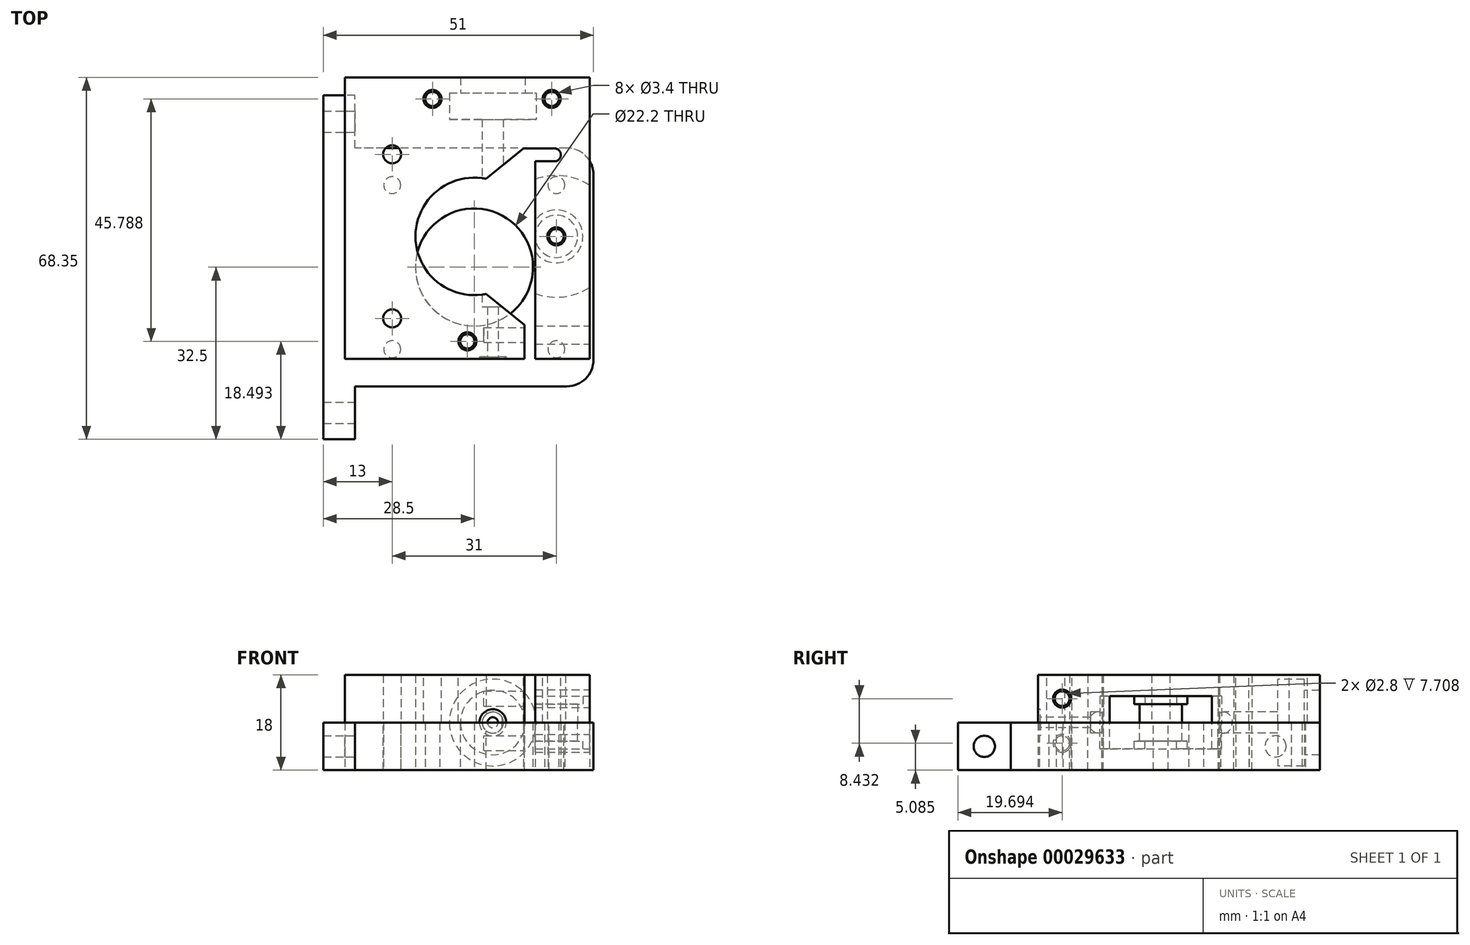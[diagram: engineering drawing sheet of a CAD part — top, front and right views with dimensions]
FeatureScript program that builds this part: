
annotation { "Feature Type Name" : "Feature", "Feature Type Description" : "" }
export const myFeature = defineFeature(function(context is Context, id is Id, definition is map)
    precondition{}
    {
        {
            var Q0;
            Q0=qCreatedBy(makeId("Top.planeOp"),FACE);
            var sketch = newSketch(context, id + "F0", { "sketchPlane" : qUnion([Q0])});
            skLineSegment(sketch, "E0", {"start": v(-24.43, 35.85) * mm, "end": v(-24.43, -17.36) * mm});
            skLineSegment(sketch, "E1", {"start": v(-24.43, -17.36) * mm, "end": v(-24.43, -17.36) * mm});
            skLineSegment(sketch, "E2", {"start": v(-24.43, -17.36) * mm, "end": v(-24.43, -17.35) * mm});
            skLineSegment(sketch, "E3", {"start": v(-24.43, -17.35) * mm, "end": v(9.48, -17.35) * mm});
            skLineSegment(sketch, "E4", {"start": v(9.48, -17.35) * mm, "end": v(9.48, 22.43) * mm});
            skLineSegment(sketch, "E5", {"start": v(9.48, 22.43) * mm, "end": v(15.14, 22.43) * mm});
            skLineSegment(sketch, "E6", {"start": v(15.14, 20) * mm, "end": v(11.48, 20) * mm});
            skLineSegment(sketch, "E7", {"start": v(11.48, 20) * mm, "end": v(11.48, -17.35) * mm});
            skLineSegment(sketch, "E8", {"start": v(11.48, -17.35) * mm, "end": v(21.77, -17.35) * mm});
            skLineSegment(sketch, "E9", {"start": v(21.77, -17.35) * mm, "end": v(21.77, 35.85) * mm});
            skLineSegment(sketch, "E10", {"start": v(21.77, 35.85) * mm, "end": v(-24.43, 35.85) * mm});
            skCircle(sketch, "E11", {"center": v(-7.89, 31.78) * mm, "radius": 1.35 * mm});
            skCircle(sketch, "E12", {"center": v(14.61, 31.78) * mm, "radius": 1.35 * mm});
            skCircle(sketch, "E13", {"center": v(-1.3, -14) * mm, "radius": 1.35 * mm});
            skArc(sketch, "E14", {"start": v(15.14, 20) * mm, "mid": v(16.35, 21.21) * mm, "end": v(15.14, 22.43) * mm});
            skCircle(sketch, "E15", {"center": v(-7.89, 31.78) * mm, "radius": 1.7 * mm});
            skCircle(sketch, "E16", {"center": v(14.61, 31.78) * mm, "radius": 1.7 * mm});
            skCircle(sketch, "E17", {"center": v(-1.3, -14) * mm, "radius": 1.7 * mm});
            skSolve(sketch);
        }
        {
            var Q0;
            Q0=makeQuery(id+"F0.imprint","IMPRINT",FACE,{"disambiguationData":[TD([[makeQuery(id+"F0.imprint","IMPRINT",EDGE,{"derivedFrom":sQuery(id+"F0.wireOp",EDGE,"E0")}),1.0]])]});
            var Q1;
            Q1=makeQuery(id+"F0.imprint","IMPRINT",FACE,{"disambiguationData":[TD([[makeQuery(id+"F0.imprint","IMPRINT",EDGE,{"derivedFrom":sQuery(id+"F0.wireOp",EDGE,"E11")}),-1.0]])]});
            var Q2;
            Q2=makeQuery(id+"F0.imprint","IMPRINT",FACE,{"disambiguationData":[TD([[makeQuery(id+"F0.imprint","IMPRINT",EDGE,{"derivedFrom":sQuery(id+"F0.wireOp",EDGE,"E12")}),-1.0]])]});
            var Q3;
            Q3=makeQuery(id+"F0.imprint","IMPRINT",FACE,{"disambiguationData":[TD([[makeQuery(id+"F0.imprint","IMPRINT",EDGE,{"derivedFrom":sQuery(id+"F0.wireOp",EDGE,"E13")}),-1.0]])]});
            extrude(context, id + "F1", {"entities" : qUnion([Q0, Q1, Q2, Q3]), "depth" : 9 * mm});
        }
        {
            var Q0;
            Q0=makeQuery(id+"F1.opExtrude","CAP_FACE",FACE,{"disambiguationData":[OSD([sQuery(id+"F0.wireOp",EDGE,"E0"),sQuery(id+"F0.wireOp",EDGE,"E1"),sQuery(id+"F0.wireOp",EDGE,"E2"),sQuery(id+"F0.wireOp",EDGE,"E3"),sQuery(id+"F0.wireOp",EDGE,"E4"),sQuery(id+"F0.wireOp",EDGE,"E5"),sQuery(id+"F0.wireOp",EDGE,"E6"),sQuery(id+"F0.wireOp",EDGE,"E7"),sQuery(id+"F0.wireOp",EDGE,"E8"),sQuery(id+"F0.wireOp",EDGE,"E9"),sQuery(id+"F0.wireOp",EDGE,"E10"),sQuery(id+"F0.wireOp",EDGE,"604cad85-587a-4b7d-8070-06f4cba85480"),sQuery(id+"F0.wireOp",EDGE,"6e5e38c1-5bff-4efe-a8c5-b84022f0a049"),sQuery(id+"F0.wireOp",EDGE,"b8144507-9dd7-4af4-87a3-7b649dd00ae6"),sQuery(id+"F0.wireOp",EDGE,"b9c2cb7c-5e58-4995-888e-a78f0403fbb5"),sQuery(id+"F0.wireOp",EDGE,"885990ab-7576-4c23-8475-595d2769e284"),sQuery(id+"F0.wireOp",EDGE,"E11"),sQuery(id+"F0.wireOp",EDGE,"E12"),sQuery(id+"F0.wireOp",EDGE,"E13"),sQuery(id+"F0.wireOp",EDGE,"E14")])],"isStart":false});
            var sketch = newSketch(context, id + "F2", { "sketchPlane" : qUnion([Q0])});
            skCircle(sketch, "E18", {"center": v(0, 5.82) * mm, "radius": 11.1 * mm});
            skCircle(sketch, "E19", {"center": v(-15.5, 21.32) * mm, "radius": 1.7 * mm});
            skCircle(sketch, "E20", {"center": v(-15.5, -9.68) * mm, "radius": 1.7 * mm});
            skSolve(sketch);
        }
        {
            var Q0;
            Q0=qSketchRegion(id+"F2",true);
            extrude(context, id + "F3", {"entities" : qUnion([Q0]), "operationType" : NewBodyOperationType.REMOVE, "endBound" : BoundingType.THROUGH_ALL, "oppositeDirection" : true, "depth" : 25 * mm});
        }
        {
            var Q0;
            Q0=makeQuery(id+"F1.opExtrude","CAP_FACE",FACE,{"disambiguationData":[OSD([sQuery(id+"F0.wireOp",EDGE,"E0"),sQuery(id+"F0.wireOp",EDGE,"E1"),sQuery(id+"F0.wireOp",EDGE,"E2"),sQuery(id+"F0.wireOp",EDGE,"E3"),sQuery(id+"F0.wireOp",EDGE,"E4"),sQuery(id+"F0.wireOp",EDGE,"E5"),sQuery(id+"F0.wireOp",EDGE,"E6"),sQuery(id+"F0.wireOp",EDGE,"E7"),sQuery(id+"F0.wireOp",EDGE,"E8"),sQuery(id+"F0.wireOp",EDGE,"E9"),sQuery(id+"F0.wireOp",EDGE,"E10"),sQuery(id+"F0.wireOp",EDGE,"604cad85-587a-4b7d-8070-06f4cba85480"),sQuery(id+"F0.wireOp",EDGE,"6e5e38c1-5bff-4efe-a8c5-b84022f0a049"),sQuery(id+"F0.wireOp",EDGE,"E11"),sQuery(id+"F0.wireOp",EDGE,"E12"),sQuery(id+"F0.wireOp",EDGE,"E13"),sQuery(id+"F0.wireOp",EDGE,"E14")])],"isStart":false});
            var sketch = newSketch(context, id + "F4", { "sketchPlane" : qUnion([Q0])});
            skCircle(sketch, "E21", {"center": v(15.5, 5.82) * mm, "radius": 11.5 * mm});
            skCircle(sketch, "E22", {"center": v(15.5, 5.82) * mm, "radius": 5 * mm});
            skCircle(sketch, "E23", {"center": v(15.5, 5.82) * mm, "radius": 4 * mm});
            skLineSegment(sketch, "E24", {"start": v(0, 5.82) * mm, "end": v(31, 5.82) * mm, "construction": true});
            skCircle(sketch, "E25", {"center": v(15.5, 5.82) * mm, "radius": 1.4 * mm});
            skCircle(sketch, "E26", {"center": v(15.5, 5.82) * mm, "radius": 1.7 * mm});
            skSolve(sketch);
        }
        {
            var Q0;
            Q0=makeQuery(id+"F4.imprint","IMPRINT",FACE,{"disambiguationData":[TD([[makeQuery(id+"F4.imprint","IMPRINT",EDGE,{"derivedFrom":sQuery(id+"F4.wireOp",EDGE,"E22")}),-1.0]])]});
            extrude(context, id + "F5", {"entities" : qUnion([Q0]), "operationType" : NewBodyOperationType.REMOVE, "oppositeDirection" : true, "depth" : 5 * mm});
        }
        {
            var Q0;
            Q0=makeQuery(id+"F4.imprint","IMPRINT",FACE,{"disambiguationData":[TD([[makeQuery(id+"F4.imprint","IMPRINT",EDGE,{"derivedFrom":sQuery(id+"F4.wireOp",EDGE,"E22")}),1.0]])]});
            var Q1;
            Q1=makeQuery(id+"F4.imprint","IMPRINT",FACE,{"disambiguationData":[TD([[makeQuery(id+"F4.imprint","IMPRINT",EDGE,{"derivedFrom":sQuery(id+"F4.wireOp",EDGE,"E23")}),-1.0]])]});
            extrude(context, id + "F6", {"entities" : qUnion([Q0, Q1]), "operationType" : NewBodyOperationType.REMOVE, "oppositeDirection" : true, "depth" : 3.5 * mm});
        }
        {
            var Q0;
            {var subQ0=sQuery(id+"F0.wireOp",EDGE,"E0");var subQ1=sQuery(id+"F0.wireOp",EDGE,"E1");var subQ2=sQuery(id+"F0.wireOp",EDGE,"E2");var subQ3=sQuery(id+"F0.wireOp",EDGE,"E3");var subQ4=sQuery(id+"F0.wireOp",EDGE,"E4");var subQ5=sQuery(id+"F0.wireOp",EDGE,"E5");var subQ6=sQuery(id+"F0.wireOp",EDGE,"E6");var subQ7=sQuery(id+"F0.wireOp",EDGE,"E7");var subQ8=sQuery(id+"F0.wireOp",EDGE,"E9");var subQ9=sQuery(id+"F0.wireOp",EDGE,"E10");var subQ10=sQuery(id+"F0.wireOp",EDGE,"604cad85-587a-4b7d-8070-06f4cba85480");var subQ11=sQuery(id+"F0.wireOp",EDGE,"6e5e38c1-5bff-4efe-a8c5-b84022f0a049");var subQ12=sQuery(id+"F0.wireOp",EDGE,"E11");var subQ13=sQuery(id+"F0.wireOp",EDGE,"E12");var subQ14=sQuery(id+"F0.wireOp",EDGE,"E13");var subQ15=sQuery(id+"F0.wireOp",EDGE,"E14");Q0=makeQuery(id+"F5.boolean.opBoolean","SPLIT",FACE,{"disambiguationData":[TD([makeQuery(id+"F1.opExtrude","SWEPT_FACE",FACE,{"disambiguationData":[OSD([subQ0])]})])],"derivedFrom":makeQuery(id+"F1.opExtrude","CAP_FACE",FACE,{"disambiguationData":[OSD([subQ0,subQ1,subQ2,subQ3,subQ4,subQ5,subQ6,subQ7,sQuery(id+"F0.wireOp",EDGE,"E8"),subQ8,subQ9,subQ10,subQ11,subQ12,subQ13,subQ14,subQ15])],"isStart":false})});}
            var sketch = newSketch(context, id + "F7", { "sketchPlane" : qUnion([Q0])});
            skLineSegment(sketch, "E27", {"start": v(3.5, 15.43) * mm, "end": v(3.5, 37.1) * mm});
            skLineSegment(sketch, "E28", {"start": v(0, 5.82) * mm, "end": v(31.4, 5.82) * mm, "construction": true});
            skLineSegment(sketch, "E29.0.MirrorCS", {"start": v(0.98, -16.94) * mm, "end": v(2.5, -16.94) * mm});
            skLineSegment(sketch, "E29.1.MirrorCS", {"start": v(3.5, -3.78) * mm, "end": v(3.5, -25.46) * mm});
            skLineSegment(sketch, "E29.2.MirrorCS", {"start": v(0.98, -25.46) * mm, "end": v(0.98, -16.94) * mm});
            skLineSegment(sketch, "E29.3.MirrorCS", {"start": v(1.5, -3.78) * mm, "end": v(3.5, -3.78) * mm});
            skLineSegment(sketch, "E29.4.MirrorCS", {"start": v(2.5, -7.47) * mm, "end": v(1.5, -7.47) * mm});
            skLineSegment(sketch, "E29.5.MirrorCS", {"start": v(2.5, -16.94) * mm, "end": v(2.5, -7.47) * mm});
            skLineSegment(sketch, "E29.6.MirrorCS", {"start": v(3.5, -25.46) * mm, "end": v(0.98, -25.46) * mm});
            skLineSegment(sketch, "E30", {"start": v(-2.6, 37.1) * mm, "end": v(-2.6, 32.9) * mm});
            skLineSegment(sketch, "E31", {"start": v(-2.6, 32.9) * mm, "end": v(-4.7, 32.9) * mm});
            skLineSegment(sketch, "E32", {"start": v(-4.7, 32.9) * mm, "end": v(-4.7, 27.9) * mm});
            skLineSegment(sketch, "E33", {"start": v(-4.7, 27.9) * mm, "end": v(1.5, 27.9) * mm});
            skLineSegment(sketch, "E34", {"start": v(-2.6, 37.1) * mm, "end": v(3.5, 37.1) * mm});
            skLineSegment(sketch, "E35", {"start": v(1.5, 27.9) * mm, "end": v(1.5, 15.43) * mm});
            skLineSegment(sketch, "E36", {"start": v(1.5, 15.43) * mm, "end": v(3.5, 15.43) * mm});
            skLineSegment(sketch, "E37", {"start": v(1.5, -7.47) * mm, "end": v(1.5, -3.78) * mm});
            skSolve(sketch);
        }
        {
            var Q0;
            Q0=qSketchRegion(id+"F7",true);
            var Q1;
            Q1=sQuery(id+"F7.wireOp",EDGE,"E27");
            revolve(context, id + "F8", {"entities" : qUnion([Q0]), "axis" : qUnion([Q1]), "revolveType" : RevolveType.FULL});
        }
        {
            var Q0;
            Q0=makeQuery(id+"F8.opRevolve","SWEPT_BODY",BODY,{"disambiguationData":[OSD([sQuery(id+"F7.wireOp",EDGE,"0e4a01cc-4869-4b9d-8ca2-1c94110d196d"),sQuery(id+"F7.wireOp",EDGE,"4d913e13-2244-4a79-84d2-82f6c5de00b3"),sQuery(id+"F7.wireOp",EDGE,"1203443b-fa58-4cec-9fe4-144960d3b7c2"),sQuery(id+"F7.wireOp",EDGE,"f73e5a92-9274-40af-91db-ab5fa52ec61f"),sQuery(id+"F7.wireOp",EDGE,"4cc6588a-36a6-4115-9f4e-735cf5f17870"),sQuery(id+"F7.wireOp",EDGE,"E27"),sQuery(id+"F7.wireOp",EDGE,"0bbee7b9-97e0-41c3-ac0e-625151f8027d")])]});
            var Q1;
            Q1=makeQuery(id+"F1.opExtrude","SWEPT_BODY",BODY,{"disambiguationData":[OSD([sQuery(id+"F0.wireOp",EDGE,"E0"),sQuery(id+"F0.wireOp",EDGE,"E1"),sQuery(id+"F0.wireOp",EDGE,"E2"),sQuery(id+"F0.wireOp",EDGE,"E3"),sQuery(id+"F0.wireOp",EDGE,"E4"),sQuery(id+"F0.wireOp",EDGE,"E5"),sQuery(id+"F0.wireOp",EDGE,"E6"),sQuery(id+"F0.wireOp",EDGE,"E7"),sQuery(id+"F0.wireOp",EDGE,"E8"),sQuery(id+"F0.wireOp",EDGE,"E9"),sQuery(id+"F0.wireOp",EDGE,"E10"),sQuery(id+"F0.wireOp",EDGE,"604cad85-587a-4b7d-8070-06f4cba85480"),sQuery(id+"F0.wireOp",EDGE,"6e5e38c1-5bff-4efe-a8c5-b84022f0a049"),sQuery(id+"F0.wireOp",EDGE,"E11"),sQuery(id+"F0.wireOp",EDGE,"E12"),sQuery(id+"F0.wireOp",EDGE,"E13"),sQuery(id+"F0.wireOp",EDGE,"E14")])]});
            booleanBodies(context, id + "F9", {"operationType" : BooleanOperationType.SUBTRACTION, "tools" : qUnion([Q0]), "targets" : qUnion([Q1]), "keepTools" : true});
        }
        {
            var Q0;
            Q0=makeQuery(id+"F8.opRevolve","SWEPT_BODY",BODY,{"disambiguationData":[OSD([sQuery(id+"F7.wireOp",EDGE,"E29.0.MirrorCS"),sQuery(id+"F7.wireOp",EDGE,"E29.1.MirrorCS"),sQuery(id+"F7.wireOp",EDGE,"E29.2.MirrorCS"),sQuery(id+"F7.wireOp",EDGE,"E29.3.MirrorCS"),sQuery(id+"F7.wireOp",EDGE,"E29.4.MirrorCS"),sQuery(id+"F7.wireOp",EDGE,"E29.5.MirrorCS"),sQuery(id+"F7.wireOp",EDGE,"E29.6.MirrorCS")])]});
            var Q1;
            Q1=makeQuery(id+"F1.opExtrude","SWEPT_BODY",BODY,{"disambiguationData":[OSD([sQuery(id+"F0.wireOp",EDGE,"E0"),sQuery(id+"F0.wireOp",EDGE,"E1"),sQuery(id+"F0.wireOp",EDGE,"E2"),sQuery(id+"F0.wireOp",EDGE,"E3"),sQuery(id+"F0.wireOp",EDGE,"E4"),sQuery(id+"F0.wireOp",EDGE,"E5"),sQuery(id+"F0.wireOp",EDGE,"E6"),sQuery(id+"F0.wireOp",EDGE,"E7"),sQuery(id+"F0.wireOp",EDGE,"E8"),sQuery(id+"F0.wireOp",EDGE,"E9"),sQuery(id+"F0.wireOp",EDGE,"E10"),sQuery(id+"F0.wireOp",EDGE,"604cad85-587a-4b7d-8070-06f4cba85480"),sQuery(id+"F0.wireOp",EDGE,"6e5e38c1-5bff-4efe-a8c5-b84022f0a049"),sQuery(id+"F0.wireOp",EDGE,"E11"),sQuery(id+"F0.wireOp",EDGE,"E12"),sQuery(id+"F0.wireOp",EDGE,"E13"),sQuery(id+"F0.wireOp",EDGE,"E14")])]});
            booleanBodies(context, id + "F10", {"operationType" : BooleanOperationType.SUBTRACTION, "tools" : qUnion([Q0]), "targets" : qUnion([Q1]), "keepTools" : true});
        }
        {
            var Q0;
            Q0=qSketchRegion(id+"F0",true);
            extrude(context, id + "F11", {"entities" : qUnion([Q0]), "oppositeDirection" : true, "depth" : 9 * mm});
        }
        {
            var Q0;
            Q0=makeQuery(id+"F11.opExtrude","SWEPT_BODY",BODY,{"disambiguationData":[OSD([sQuery(id+"F0.wireOp",EDGE,"E0"),sQuery(id+"F0.wireOp",EDGE,"E3"),sQuery(id+"F0.wireOp",EDGE,"E4"),sQuery(id+"F0.wireOp",EDGE,"E5"),sQuery(id+"F0.wireOp",EDGE,"E6"),sQuery(id+"F0.wireOp",EDGE,"E7"),sQuery(id+"F0.wireOp",EDGE,"E8"),sQuery(id+"F0.wireOp",EDGE,"E9"),sQuery(id+"F0.wireOp",EDGE,"E10"),sQuery(id+"F0.wireOp",EDGE,"E11"),sQuery(id+"F0.wireOp",EDGE,"E12"),sQuery(id+"F0.wireOp",EDGE,"E13"),sQuery(id+"F0.wireOp",EDGE,"E14")])]});
            transform(context, id + "F12", {"entities" : qUnion([Q0]), "transformType" : TransformType.TRANSLATION_3D, "dx" : 0 * mm, "dy" : 0 * mm, "dz" : 18 * mm, "makeCopy" : false});
        }
        {
            var Q0;
            Q0=qSketchRegion(id+"F2",true);
            extrude(context, id + "F13", {"entities" : qUnion([Q0]), "operationType" : NewBodyOperationType.REMOVE, "endBound" : BoundingType.THROUGH_ALL, "depth" : 25 * mm});
        }
        {
            var Q0;
            {var subQ3=sQuery(id+"F4.wireOp",EDGE,"E21");var subQ7=makeQuery(id+"F1.opExtrude","CAP_EDGE",EDGE,{"disambiguationData":[OSD([sQuery(id+"F0.wireOp",EDGE,"E9")])],"isStart":false});var subQ9=makeQuery(id+"F4.imprint","INTERSECT",VERTEX,{"disambiguationData":[OD(0.0)],"derivedFrom":[subQ7,subQ3]});Q0=makeQuery(id+"F4.imprint","IMPRINT",FACE,{"disambiguationData":[TD([[makeQuery(id+"F4.imprint","IMPRINT",EDGE,{"disambiguationData":[TD([[subQ9,-1.0]])],"derivedFrom":subQ3}),1.0]])]});}
            extrude(context, id + "F14", {"entities" : qUnion([Q0]), "operationType" : NewBodyOperationType.REMOVE, "depth" : 5 * mm});
        }
        {
            var Q0;
            Q0=makeQuery(id+"F4.imprint","IMPRINT",FACE,{"disambiguationData":[TD([[makeQuery(id+"F4.imprint","IMPRINT",EDGE,{"derivedFrom":sQuery(id+"F4.wireOp",EDGE,"E23")}),-1.0]])]});
            extrude(context, id + "F15", {"entities" : qUnion([Q0]), "operationType" : NewBodyOperationType.REMOVE, "depth" : 3.5 * mm});
        }
        {
            var Q0;
            Q0=makeQuery(id+"F8.opRevolve","SWEPT_BODY",BODY,{"disambiguationData":[OSD([sQuery(id+"F7.wireOp",EDGE,"0e4a01cc-4869-4b9d-8ca2-1c94110d196d"),sQuery(id+"F7.wireOp",EDGE,"4d913e13-2244-4a79-84d2-82f6c5de00b3"),sQuery(id+"F7.wireOp",EDGE,"1203443b-fa58-4cec-9fe4-144960d3b7c2"),sQuery(id+"F7.wireOp",EDGE,"f73e5a92-9274-40af-91db-ab5fa52ec61f"),sQuery(id+"F7.wireOp",EDGE,"4cc6588a-36a6-4115-9f4e-735cf5f17870"),sQuery(id+"F7.wireOp",EDGE,"E27"),sQuery(id+"F7.wireOp",EDGE,"0bbee7b9-97e0-41c3-ac0e-625151f8027d")])]});
            var Q1;
            Q1=makeQuery(id+"F11.opExtrude","SWEPT_BODY",BODY,{"disambiguationData":[OSD([sQuery(id+"F0.wireOp",EDGE,"E0"),sQuery(id+"F0.wireOp",EDGE,"E3"),sQuery(id+"F0.wireOp",EDGE,"E4"),sQuery(id+"F0.wireOp",EDGE,"E5"),sQuery(id+"F0.wireOp",EDGE,"E6"),sQuery(id+"F0.wireOp",EDGE,"E7"),sQuery(id+"F0.wireOp",EDGE,"E8"),sQuery(id+"F0.wireOp",EDGE,"E9"),sQuery(id+"F0.wireOp",EDGE,"E10"),sQuery(id+"F0.wireOp",EDGE,"E11"),sQuery(id+"F0.wireOp",EDGE,"E12"),sQuery(id+"F0.wireOp",EDGE,"E13"),sQuery(id+"F0.wireOp",EDGE,"E14")])]});
            booleanBodies(context, id + "F16", {"operationType" : BooleanOperationType.SUBTRACTION, "tools" : qUnion([Q0]), "targets" : qUnion([Q1])});
        }
        {
            var Q0;
            Q0=makeQuery(id+"F8.opRevolve","SWEPT_BODY",BODY,{"disambiguationData":[OSD([sQuery(id+"F7.wireOp",EDGE,"E29.0.MirrorCS"),sQuery(id+"F7.wireOp",EDGE,"E29.1.MirrorCS"),sQuery(id+"F7.wireOp",EDGE,"E29.2.MirrorCS"),sQuery(id+"F7.wireOp",EDGE,"E29.3.MirrorCS"),sQuery(id+"F7.wireOp",EDGE,"E29.4.MirrorCS"),sQuery(id+"F7.wireOp",EDGE,"E29.5.MirrorCS"),sQuery(id+"F7.wireOp",EDGE,"E29.6.MirrorCS")])]});
            var Q1;
            Q1=makeQuery(id+"F11.opExtrude","SWEPT_BODY",BODY,{"disambiguationData":[OSD([sQuery(id+"F0.wireOp",EDGE,"E0"),sQuery(id+"F0.wireOp",EDGE,"E3"),sQuery(id+"F0.wireOp",EDGE,"E4"),sQuery(id+"F0.wireOp",EDGE,"E5"),sQuery(id+"F0.wireOp",EDGE,"E6"),sQuery(id+"F0.wireOp",EDGE,"E7"),sQuery(id+"F0.wireOp",EDGE,"E8"),sQuery(id+"F0.wireOp",EDGE,"E9"),sQuery(id+"F0.wireOp",EDGE,"E10"),sQuery(id+"F0.wireOp",EDGE,"E11"),sQuery(id+"F0.wireOp",EDGE,"E12"),sQuery(id+"F0.wireOp",EDGE,"E13"),sQuery(id+"F0.wireOp",EDGE,"E14")])]});
            booleanBodies(context, id + "F17", {"operationType" : BooleanOperationType.SUBTRACTION, "tools" : qUnion([Q0]), "targets" : qUnion([Q1])});
        }
        {
            var Q0;
            Q0=makeQuery(id+"F11.opExtrude","SWEPT_FACE",FACE,{"disambiguationData":[OSD([sQuery(id+"F0.wireOp",EDGE,"E9")])]});
            var sketch = newSketch(context, id + "F18", { "sketchPlane" : qUnion([Q0])});
            skCircle(sketch, "E38", {"center": v(-12.8, 13.52) * mm, "radius": 1.7 * mm});
            skCircle(sketch, "E39", {"center": v(-12.8, 13.52) * mm, "radius": 1.4 * mm});
            skCircle(sketch, "E40", {"center": v(-12.8, 5.09) * mm, "radius": 1.7 * mm});
            skCircle(sketch, "E41", {"center": v(-12.8, 5.09) * mm, "radius": 1.4 * mm});
            skSolve(sketch);
        }
        {
            var Q0;
            Q0=makeQuery(id+"F18.imprint","IMPRINT",FACE,{"disambiguationData":[TD([[makeQuery(id+"F18.imprint","IMPRINT",EDGE,{"derivedFrom":sQuery(id+"F18.wireOp",EDGE,"E39")}),1.0]])]});
            extrude(context, id + "F19", {"entities" : qUnion([Q0]), "operationType" : NewBodyOperationType.REMOVE, "oppositeDirection" : true, "depth" : 20 * mm});
        }
        {
            var Q0;
            Q0=makeQuery(id+"F18.imprint","IMPRINT",FACE,{"disambiguationData":[TD([[makeQuery(id+"F18.imprint","IMPRINT",EDGE,{"derivedFrom":sQuery(id+"F18.wireOp",EDGE,"E38")}),1.0]])]});
            extrude(context, id + "F20", {"entities" : qUnion([Q0]), "operationType" : NewBodyOperationType.REMOVE, "oppositeDirection" : true, "depth" : 11 * mm});
        }
        {
            var Q0;
            Q0=makeQuery(id+"F18.imprint","IMPRINT",FACE,{"disambiguationData":[TD([[makeQuery(id+"F18.imprint","IMPRINT",EDGE,{"derivedFrom":sQuery(id+"F18.wireOp",EDGE,"E41")}),1.0]])]});
            extrude(context, id + "F21", {"entities" : qUnion([Q0]), "operationType" : NewBodyOperationType.REMOVE, "oppositeDirection" : true, "depth" : 20 * mm});
        }
        {
            var Q0;
            Q0=makeQuery(id+"F18.imprint","IMPRINT",FACE,{"disambiguationData":[TD([[makeQuery(id+"F18.imprint","IMPRINT",EDGE,{"derivedFrom":sQuery(id+"F18.wireOp",EDGE,"E40")}),1.0]])]});
            extrude(context, id + "F22", {"entities" : qUnion([Q0]), "operationType" : NewBodyOperationType.REMOVE, "oppositeDirection" : true, "depth" : 11 * mm});
        }
        {
            var Q0;
            Q0=makeQuery(id+"F4.imprint","IMPRINT",FACE,{"disambiguationData":[TD([[makeQuery(id+"F4.imprint","IMPRINT",EDGE,{"derivedFrom":sQuery(id+"F4.wireOp",EDGE,"E25")}),1.0]])]});
            extrude(context, id + "F23", {"entities" : qUnion([Q0]), "operationType" : NewBodyOperationType.REMOVE, "endBound" : BoundingType.THROUGH_ALL, "oppositeDirection" : true, "depth" : 25 * mm});
        }
        {
            var Q0;
            Q0=makeQuery(id+"F4.imprint","IMPRINT",FACE,{"disambiguationData":[TD([[makeQuery(id+"F4.imprint","IMPRINT",EDGE,{"derivedFrom":sQuery(id+"F4.wireOp",EDGE,"E25")}),1.0]])]});
            var Q1;
            Q1=makeQuery(id+"F4.imprint","IMPRINT",FACE,{"disambiguationData":[TD([[makeQuery(id+"F4.imprint","IMPRINT",EDGE,{"derivedFrom":sQuery(id+"F4.wireOp",EDGE,"E25")}),-1.0]])]});
            extrude(context, id + "F24", {"entities" : qUnion([Q0, Q1]), "operationType" : NewBodyOperationType.REMOVE, "endBound" : BoundingType.THROUGH_ALL, "depth" : 25 * mm});
        }
        {
            var Q0;
            Q0=makeQuery(id+"F3.boolean.opBoolean","INTERSECT",EDGE,{"disambiguationData":[OD(0.0)],"derivedFrom":[makeQuery(id+"F1.opExtrude","SWEPT_FACE",FACE,{"disambiguationData":[OSD([sQuery(id+"F0.wireOp",EDGE,"E4")])]}),makeQuery(id+"F3.opExtrude","SWEPT_FACE",FACE,{"disambiguationData":[OSD([sQuery(id+"F2.wireOp",EDGE,"E18")])]})]});
            var Q1;
            Q1=makeQuery(id+"F3.boolean.opBoolean","INTERSECT",EDGE,{"disambiguationData":[OD(1.0)],"derivedFrom":[makeQuery(id+"F1.opExtrude","SWEPT_FACE",FACE,{"disambiguationData":[OSD([sQuery(id+"F0.wireOp",EDGE,"E4")])]}),makeQuery(id+"F3.opExtrude","SWEPT_FACE",FACE,{"disambiguationData":[OSD([sQuery(id+"F2.wireOp",EDGE,"E18")])]})]});
            var Q2;
            Q2=makeQuery(id+"F13.boolean.opBoolean","INTERSECT",EDGE,{"disambiguationData":[OD(1.0)],"derivedFrom":[makeQuery(id+"F11.opExtrude","SWEPT_FACE",FACE,{"disambiguationData":[OSD([sQuery(id+"F0.wireOp",EDGE,"E4")])]}),makeQuery(id+"F13.opExtrude","SWEPT_FACE",FACE,{"disambiguationData":[OSD([sQuery(id+"F2.wireOp",EDGE,"E18")])]})]});
            var Q3;
            Q3=makeQuery(id+"F13.boolean.opBoolean","INTERSECT",EDGE,{"disambiguationData":[OD(0.0)],"derivedFrom":[makeQuery(id+"F11.opExtrude","SWEPT_FACE",FACE,{"disambiguationData":[OSD([sQuery(id+"F0.wireOp",EDGE,"E4")])]}),makeQuery(id+"F13.opExtrude","SWEPT_FACE",FACE,{"disambiguationData":[OSD([sQuery(id+"F2.wireOp",EDGE,"E18")])]})]});
            chamfer(context, id + "F25", {"entities" : qUnion([Q0, Q1, Q2, Q3]), "width" : 6 * mm, "tangentPropagation" : true});
        }
        {
            var Q0;
            Q0=qCreatedBy(makeId("Top.planeOp"),FACE);
            var sketch = newSketch(context, id + "F26", { "sketchPlane" : qUnion([Q0])});
            skLineSegment(sketch, "E42.bottom", {"start": v(22.5, 22.5) * mm, "end": v(-22.5, 22.5) * mm});
            skLineSegment(sketch, "E42.top", {"start": v(22.5, -22.5) * mm, "end": v(-22.5, -22.5) * mm});
            skLineSegment(sketch, "E42.left", {"start": v(22.5, 22.5) * mm, "end": v(22.5, -22.5) * mm});
            skLineSegment(sketch, "E42.right", {"start": v(-22.5, 22.5) * mm, "end": v(-22.5, -22.5) * mm});
            skPoint(sketch, "E42.middle", {"position": v(0, 0) * mm});
            skCircle(sketch, "E43", {"center": v(-15.5, 15.5) * mm, "radius": 1.6 * mm});
            skCircle(sketch, "E44.0.1.0", {"center": v(-15.5, -15.5) * mm, "radius": 1.6 * mm});
            skCircle(sketch, "E44.1.0.0", {"center": v(15.5, 15.5) * mm, "radius": 1.6 * mm});
            skCircle(sketch, "E44.1.1.0", {"center": v(15.5, -15.5) * mm, "radius": 1.6 * mm});
            skLineSegment(sketch, "E44.direction1", {"start": v(-15.5, 15.5) * mm, "end": v(15.5, 15.5) * mm, "construction": true});
            skLineSegment(sketch, "E44.direction2", {"start": v(-15.5, 15.5) * mm, "end": v(-15.5, -15.5) * mm, "construction": true});
            skLineSegment(sketch, "E45", {"start": v(-22.5, 22.5) * mm, "end": v(-22.5, 32.5) * mm});
            skLineSegment(sketch, "E46", {"start": v(-22.5, 32.5) * mm, "end": v(-28.5, 32.5) * mm});
            skLineSegment(sketch, "E47", {"start": v(-28.5, 32.5) * mm, "end": v(-28.5, -32.5) * mm});
            skLineSegment(sketch, "E48", {"start": v(-28.5, -32.5) * mm, "end": v(-22.5, -32.5) * mm});
            skLineSegment(sketch, "E49", {"start": v(-22.5, -32.5) * mm, "end": v(-22.5, -22.5) * mm});
            skCircle(sketch, "E50", {"center": v(0, 0) * mm, "radius": 11.1 * mm});
            skSolve(sketch);
        }
        {
            var Q0;
            Q0=makeQuery(id+"F26.imprint","IMPRINT",FACE,{"disambiguationData":[TD([[makeQuery(id+"F26.imprint","IMPRINT",EDGE,{"derivedFrom":sQuery(id+"F26.wireOp",EDGE,"E42.right")}),-1.0]])]});
            var Q1;
            Q1=makeQuery(id+"F26.imprint","IMPRINT",FACE,{"disambiguationData":[TD([[makeQuery(id+"F26.imprint","IMPRINT",EDGE,{"derivedFrom":sQuery(id+"F26.wireOp",EDGE,"E42.bottom")}),1.0]])]});
            extrude(context, id + "F27", {"entities" : qUnion([Q0, Q1]), "depth" : 9 * mm});
        }
        {
            var Q0;
            Q0=makeQuery(id+"F27.opExtrude","SWEPT_EDGE",EDGE,{"disambiguationData":[OSD([sQuery(id+"F26.wireOp",EDGE,"E42.top"),sQuery(id+"F26.wireOp",EDGE,"E42.left")])]});
            var Q1;
            Q1=makeQuery(id+"F27.opExtrude","SWEPT_EDGE",EDGE,{"disambiguationData":[OSD([sQuery(id+"F26.wireOp",EDGE,"E42.bottom"),sQuery(id+"F26.wireOp",EDGE,"E42.left")])]});
            fillet(context, id + "F28", {"entities" : qUnion([Q0, Q1]), "radius" : 5 * mm, "tangentPropagation" : true, "allowEdgeOverflow" : false});
        }
        {
            var Q0;
            Q0=makeQuery(id+"F27.opExtrude","SWEPT_FACE",FACE,{"disambiguationData":[OSD([sQuery(id+"F26.wireOp",EDGE,"E45")])]});
            var sketch = newSketch(context, id + "F29", { "sketchPlane" : qUnion([Q0])});
            skCircle(sketch, "E51", {"center": v(-27.5, 4.5) * mm, "radius": 2 * mm});
            skPoint(sketch, "E51.centerSnap0", {"position": v(-32.5, 4.5) * mm});
            skPoint(sketch, "E51.centerSnap1", {"position": v(-27.5, 9) * mm});
            skCircle(sketch, "E52", {"center": v(27.5, 4.5) * mm, "radius": 2 * mm});
            skPoint(sketch, "E52.centerSnap0", {"position": v(32.5, 4.5) * mm});
            skPoint(sketch, "E52.centerSnap1", {"position": v(27.5, 9) * mm});
            skSolve(sketch);
        }
        {
            var Q0;
            Q0=makeQuery(id+"F29.imprint","IMPRINT",FACE,{"disambiguationData":[TD([[makeQuery(id+"F29.imprint","IMPRINT",EDGE,{"derivedFrom":sQuery(id+"F29.wireOp",EDGE,"E52")}),1.0]])]});
            var Q1;
            Q1=makeQuery(id+"F29.imprint","IMPRINT",FACE,{"disambiguationData":[TD([[makeQuery(id+"F29.imprint","IMPRINT",EDGE,{"derivedFrom":sQuery(id+"F29.wireOp",EDGE,"E51")}),1.0]])]});
            extrude(context, id + "F30", {"entities" : qUnion([Q0, Q1]), "operationType" : NewBodyOperationType.REMOVE, "endBound" : BoundingType.THROUGH_ALL, "oppositeDirection" : true, "depth" : 25 * mm});
        }
    });
